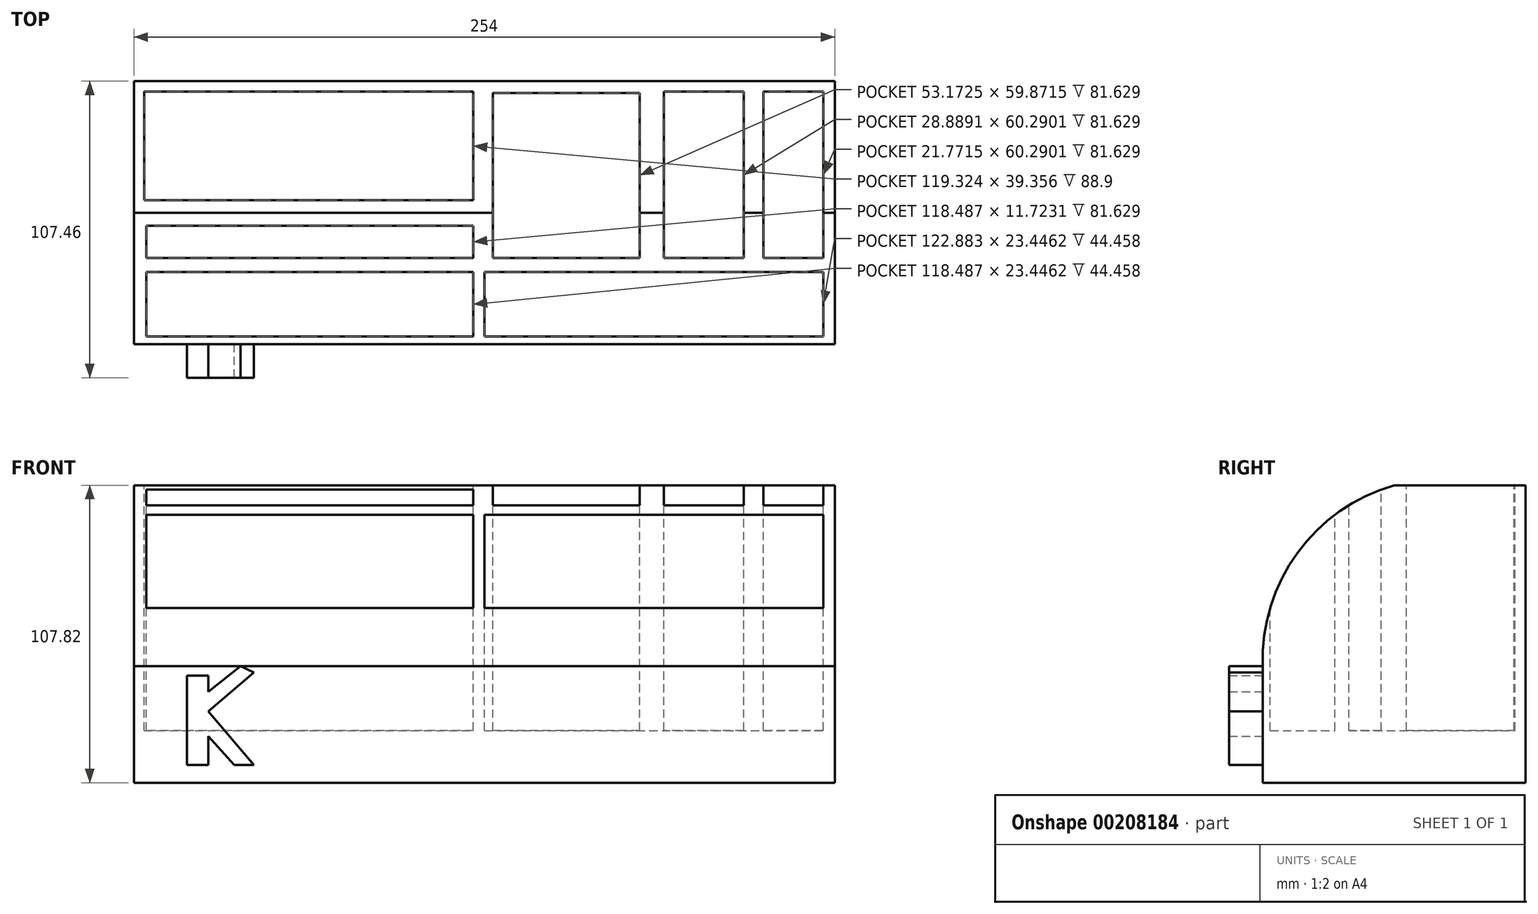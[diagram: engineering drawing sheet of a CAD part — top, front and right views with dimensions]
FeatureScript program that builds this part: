
annotation { "Feature Type Name" : "Feature", "Feature Type Description" : "" }
export const myFeature = defineFeature(function(context is Context, id is Id, definition is map)
    precondition{}
    {
        {
            var Q0;
            Q0=qCreatedBy(makeId("Right.planeOp"),FACE);
            var sketch = newSketch(context, id + "F0", { "sketchPlane" : qUnion([Q0])});
            skLineSegment(sketch, "E0.top", {"start": v(-37.65, -58.9) * mm, "end": v(57.62, -58.9) * mm});
            skLineSegment(sketch, "E0.left", {"start": v(-37.65, -16.4) * mm, "end": v(-37.65, -58.9) * mm});
            skLineSegment(sketch, "E0.right", {"start": v(57.62, 48.92) * mm, "end": v(57.62, -58.9) * mm});
            skArc(sketch, "E1", {"start": v(9.98, 48.92) * mm, "mid": v(-25.15, 24.33) * mm, "end": v(-37.65, -16.69) * mm});
            skLineSegment(sketch, "E2", {"start": v(9.98, 48.92) * mm, "end": v(57.62, 48.92) * mm});
            skSolve(sketch);
        }
        {
            var Q0;
            {var subQ2=sQuery(id+"F0.wireOp",EDGE,"E0.top");Q0=makeQuery(id+"F0.imprint","IMPRINT",FACE,{"disambiguationData":[TD([[makeQuery(id+"F0.imprint","IMPRINT",EDGE,{"derivedFrom":subQ2}),1.0]])]});}
            extrude(context, id + "F1", {"entities" : qUnion([Q0]), "endBound" : BoundingType.SYMMETRIC, "depth" : 254 * mm});
        }
        {
            var Q0;
            Q0=makeQuery(id+"F1.opExtrude","SWEPT_FACE",FACE,{"disambiguationData":[OSD([sQuery(id+"F0.wireOp",EDGE,"E2")])]});
            var sketch = newSketch(context, id + "F2", { "sketchPlane" : qUnion([Q0])});
            skLineSegment(sketch, "E3.bottom", {"start": v(-123.3, 53.8) * mm, "end": v(-3.98, 53.8) * mm});
            skLineSegment(sketch, "E3.top", {"start": v(-123.3, 14.44) * mm, "end": v(-3.98, 14.44) * mm});
            skLineSegment(sketch, "E3.left", {"start": v(-123.3, 53.8) * mm, "end": v(-123.3, 14.44) * mm});
            skLineSegment(sketch, "E3.right", {"start": v(-3.98, 53.8) * mm, "end": v(-3.98, 14.44) * mm});
            skLineSegment(sketch, "E4.bottom", {"start": v(-3.98, 5.23) * mm, "end": v(-122.46, 5.23) * mm});
            skLineSegment(sketch, "E4.top", {"start": v(-3.98, -6.49) * mm, "end": v(-122.46, -6.49) * mm});
            skLineSegment(sketch, "E4.left", {"start": v(-3.98, 5.23) * mm, "end": v(-3.98, -6.49) * mm});
            skLineSegment(sketch, "E4.right", {"start": v(-122.46, 5.23) * mm, "end": v(-122.46, -6.49) * mm});
            skLineSegment(sketch, "E5.bottom", {"start": v(-122.46, -11.51) * mm, "end": v(-3.98, -11.51) * mm});
            skLineSegment(sketch, "E5.top", {"start": v(-122.46, -34.96) * mm, "end": v(-3.98, -34.96) * mm});
            skLineSegment(sketch, "E5.left", {"start": v(-122.46, -11.51) * mm, "end": v(-122.46, -34.96) * mm});
            skLineSegment(sketch, "E5.right", {"start": v(-3.98, -11.51) * mm, "end": v(-3.98, -34.96) * mm});
            skLineSegment(sketch, "E6.bottom", {"start": v(0, -34.96) * mm, "end": v(122.88, -34.96) * mm});
            skLineSegment(sketch, "E6.top", {"start": v(0, -11.51) * mm, "end": v(122.88, -11.51) * mm});
            skLineSegment(sketch, "E6.left", {"start": v(0, -34.96) * mm, "end": v(0, -11.51) * mm});
            skLineSegment(sketch, "E6.right", {"start": v(122.88, -34.96) * mm, "end": v(122.88, -11.51) * mm});
            skLineSegment(sketch, "E7.bottom", {"start": v(122.88, -6.49) * mm, "end": v(101.11, -6.49) * mm});
            skLineSegment(sketch, "E7.top", {"start": v(122.88, 53.8) * mm, "end": v(101.11, 53.8) * mm});
            skLineSegment(sketch, "E7.left", {"start": v(122.88, -6.49) * mm, "end": v(122.88, 53.8) * mm});
            skLineSegment(sketch, "E7.right", {"start": v(101.11, -6.49) * mm, "end": v(101.11, 53.8) * mm});
            skLineSegment(sketch, "E8.bottom", {"start": v(94, -6.49) * mm, "end": v(65.1, -6.49) * mm});
            skLineSegment(sketch, "E8.top", {"start": v(94, 53.8) * mm, "end": v(65.1, 53.8) * mm});
            skLineSegment(sketch, "E8.left", {"start": v(94, -6.49) * mm, "end": v(94, 53.8) * mm});
            skLineSegment(sketch, "E8.right", {"start": v(65.1, -6.49) * mm, "end": v(65.1, 53.8) * mm});
            skLineSegment(sketch, "E9.bottom", {"start": v(56.31, -6.49) * mm, "end": v(3.14, -6.49) * mm});
            skLineSegment(sketch, "E9.top", {"start": v(56.31, 53.38) * mm, "end": v(3.14, 53.38) * mm});
            skLineSegment(sketch, "E9.left", {"start": v(56.31, -6.49) * mm, "end": v(56.31, 53.38) * mm});
            skLineSegment(sketch, "E9.right", {"start": v(3.14, -6.49) * mm, "end": v(3.14, 53.38) * mm});
            skSolve(sketch);
        }
        {
            var Q0;
            Q0 = qSketchRegion(id + "F2", true);
            extrude(context, id + "F3", {"entities" : qUnion([Q0]), "operationType" : NewBodyOperationType.REMOVE, "oppositeDirection" : true, "depth" : 88.9 * mm});
        }
        {
            var Q0;
            Q0=makeQuery(id+"F1.opExtrude","SWEPT_FACE",FACE,{"disambiguationData":[OSD([sQuery(id+"F0.wireOp",EDGE,"E0.left")])]});
            var sketch = newSketch(context, id + "F4", { "sketchPlane" : qUnion([Q0])});
            skLineSegment(sketch, "E10", {"start": v(-107.78, -20.04) * mm, "end": v(-107.78, -52.4) * mm});
            skLineSegment(sketch, "E11", {"start": v(-107.78, -52.4) * mm, "end": v(-100.01, -52.4) * mm});
            skLineSegment(sketch, "E12", {"start": v(-100.01, -42.05) * mm, "end": v(-100.01, -52.4) * mm});
            skLineSegment(sketch, "E13", {"start": v(-100.01, -42.05) * mm, "end": v(-90.63, -52.4) * mm});
            skLineSegment(sketch, "E14", {"start": v(-90.63, -52.4) * mm, "end": v(-83.5, -52.4) * mm});
            skLineSegment(sketch, "E15", {"start": v(-83.5, -52.4) * mm, "end": v(-100.01, -32.99) * mm});
            skLineSegment(sketch, "E16", {"start": v(-100.01, -32.99) * mm, "end": v(-83.5, -18.96) * mm});
            skLineSegment(sketch, "E17", {"start": v(-107.78, -20.04) * mm, "end": v(-100.01, -20.04) * mm});
            skLineSegment(sketch, "E18", {"start": v(-100.01, -20.04) * mm, "end": v(-100.01, -25.87) * mm});
            skLineSegment(sketch, "E19", {"start": v(-100.01, -25.87) * mm, "end": v(-88.36, -16.69) * mm});
            skLineSegment(sketch, "E20", {"start": v(-88.36, -16.69) * mm, "end": v(-83.5, -18.96) * mm});
            skSolve(sketch);
        }
        {
            var Q0;
            Q0=makeQuery(id+"F4.imprint","IMPRINT",FACE,{"disambiguationData":[TD([[makeQuery(id+"F4.imprint","IMPRINT",EDGE,{"derivedFrom":sQuery(id+"F4.wireOp",EDGE,"E10")}),1.0]])]});
            extrude(context, id + "F5", {"entities" : qUnion([Q0]), "operationType" : NewBodyOperationType.ADD, "depth" : 12.2 * mm});
        }
    });
